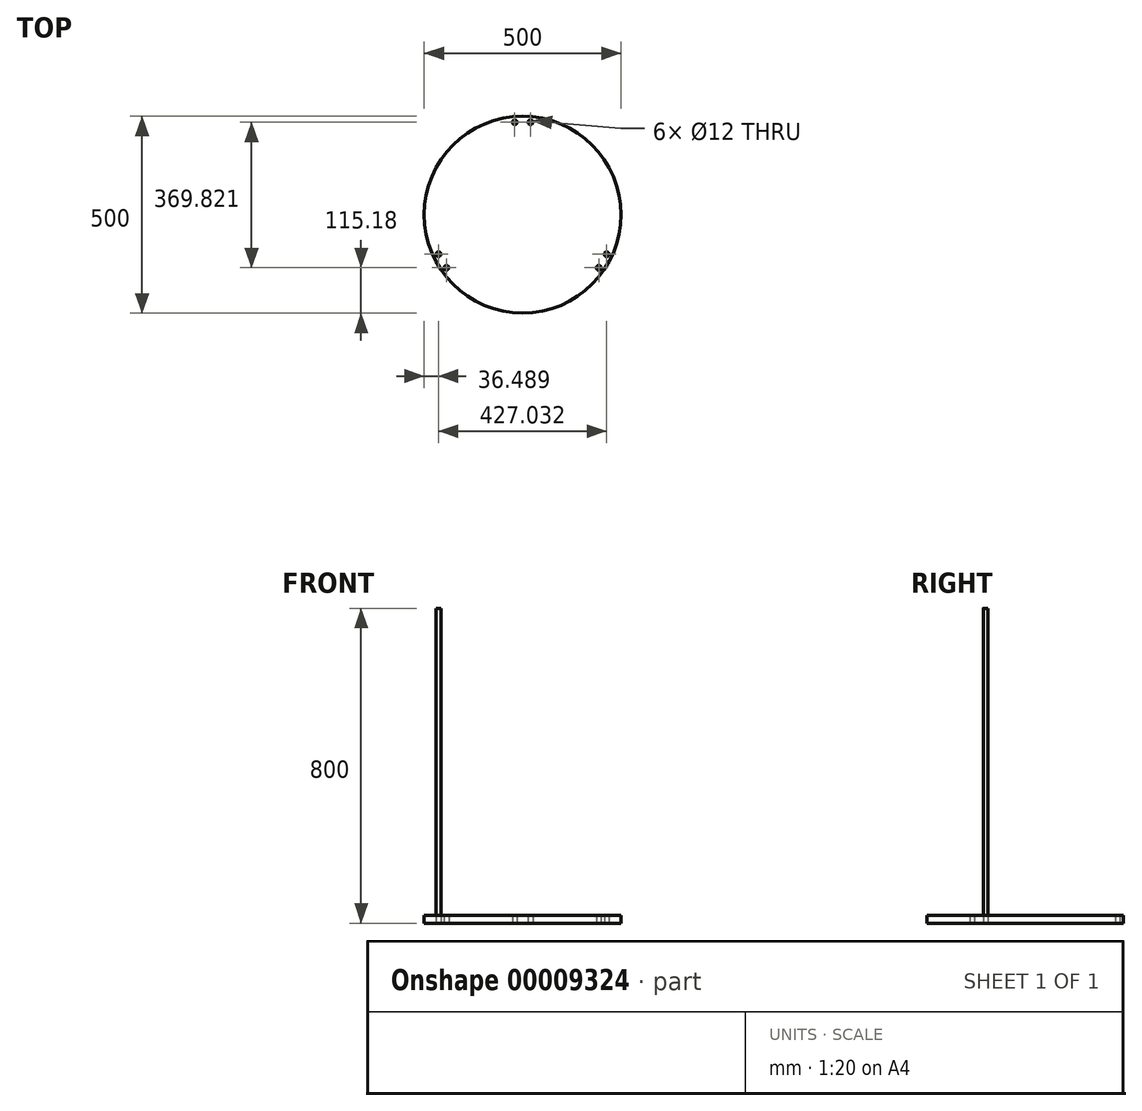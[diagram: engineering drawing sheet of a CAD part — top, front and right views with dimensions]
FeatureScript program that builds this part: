
annotation { "Feature Type Name" : "Feature", "Feature Type Description" : "" }
export const myFeature = defineFeature(function(context is Context, id is Id, definition is map)
    precondition{}
    {
        {
            var Q0;
            Q0=qCreatedBy(makeId("Top.planeOp"),FACE);
            var sketch = newSketch(context, id + "F0", { "sketchPlane" : qUnion([Q0])});
            skCircle(sketch, "E0", {"center": v(-8, -8.03) * mm, "radius": 250 * mm});
            skLineSegment(sketch, "E1", {"start": v(-8, -8.03) * mm, "end": v(-8, 241.97) * mm, "construction": true});
            skLineSegment(sketch, "E2", {"start": v(-8, -8.03) * mm, "end": v(208.5, -133.03) * mm, "construction": true});
            skLineSegment(sketch, "E3", {"start": v(-8, -8.03) * mm, "end": v(-224.51, -133.03) * mm, "construction": true});
            skCircle(sketch, "E4", {"center": v(-8, -8.03) * mm, "radius": 235 * mm, "construction": true});
            skLineSegment(sketch, "E5", {"start": v(12, 226.97) * mm, "end": v(-8, 226.97) * mm, "construction": true});
            skCircle(sketch, "E6", {"center": v(12, 226.97) * mm, "radius": 6 * mm});
            skCircle(sketch, "E7", {"center": v(-28, 226.97) * mm, "radius": 6 * mm});
            skLineSegment(sketch, "E8", {"start": v(195.51, -125.53) * mm, "end": v(205.51, -108.2) * mm, "construction": true});
            skCircle(sketch, "E9", {"center": v(205.51, -108.2) * mm, "radius": 6 * mm});
            skCircle(sketch, "E10", {"center": v(185.51, -142.85) * mm, "radius": 6 * mm});
            skLineSegment(sketch, "E11", {"start": v(-211.52, -125.53) * mm, "end": v(-221.52, -108.2) * mm, "construction": true});
            skCircle(sketch, "E12", {"center": v(-221.52, -108.2) * mm, "radius": 6 * mm});
            skCircle(sketch, "E13", {"center": v(-201.52, -142.85) * mm, "radius": 6 * mm});
            skSolve(sketch);
        }
        {
            var Q0;
            Q0=makeQuery(id+"F0.imprint","IMPRINT",FACE,{"disambiguationData":[TD([[makeQuery(id+"F0.imprint","IMPRINT",EDGE,{"derivedFrom":sQuery(id+"F0.wireOp",EDGE,"E0")}),1.0]])]});
            extrude(context, id + "F1", {"entities" : qUnion([Q0]), "depth" : 20 * mm});
        }
        {
            var Q0;
            Q0=makeQuery(id+"F0.imprint","IMPRINT",FACE,{"disambiguationData":[TD([[makeQuery(id+"F0.imprint","IMPRINT",EDGE,{"derivedFrom":sQuery(id+"F0.wireOp",EDGE,"E12")}),1.0]])]});
            extrude(context, id + "F2", {"entities" : qUnion([Q0]), "depth" : 800 * mm});
        }
    });
